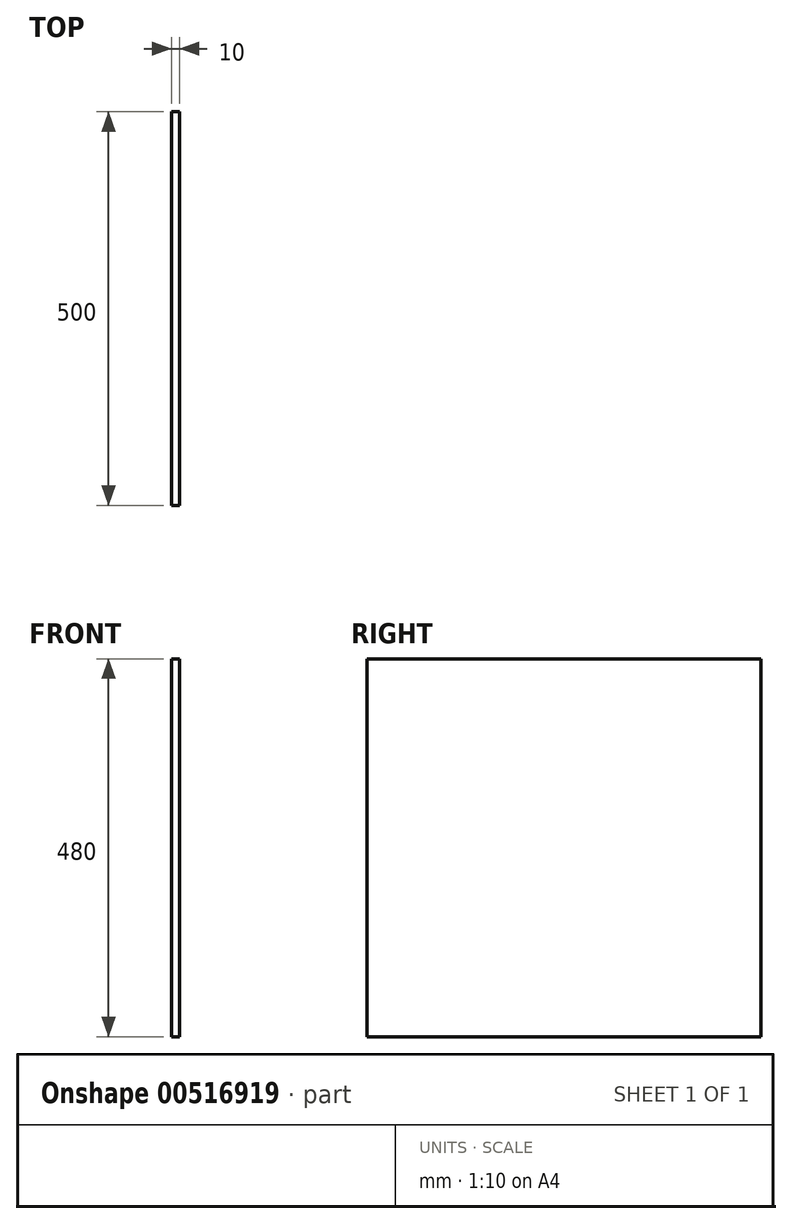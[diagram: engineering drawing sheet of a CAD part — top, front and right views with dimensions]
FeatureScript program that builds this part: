
annotation { "Feature Type Name" : "Feature", "Feature Type Description" : "" }
export const myFeature = defineFeature(function(context is Context, id is Id, definition is map)
    precondition{}
    {
        {
            var Q0;
            Q0=qCreatedBy(makeId("Right.planeOp"),FACE);
            var sketch = newSketch(context, id + "F0", { "sketchPlane" : qUnion([Q0])});
            skLineSegment(sketch, "E0.bottom", {"start": v(-250, 240) * mm, "end": v(250, 240) * mm});
            skLineSegment(sketch, "E0.top", {"start": v(-250, -240) * mm, "end": v(250, -240) * mm});
            skLineSegment(sketch, "E0.left", {"start": v(-250, 240) * mm, "end": v(-250, -240) * mm});
            skLineSegment(sketch, "E0.right", {"start": v(250, 240) * mm, "end": v(250, -240) * mm});
            skPoint(sketch, "E0.middle", {"position": v(0, 0) * mm});
            skSolve(sketch);
        }
        {
            var Q0;
            Q0=makeQuery(id+"F0.imprint","IMPRINT",FACE,{"disambiguationData":[TD([[makeQuery(id+"F0.imprint","IMPRINT",EDGE,{"derivedFrom":sQuery(id+"F0.wireOp",EDGE,"E0.bottom")}),-1.0]])]});
            extrude(context, id + "F1", {"entities" : qUnion([Q0]), "depth" : 10 * mm, "offsetDistance" : 25 * mm});
        }
    });
